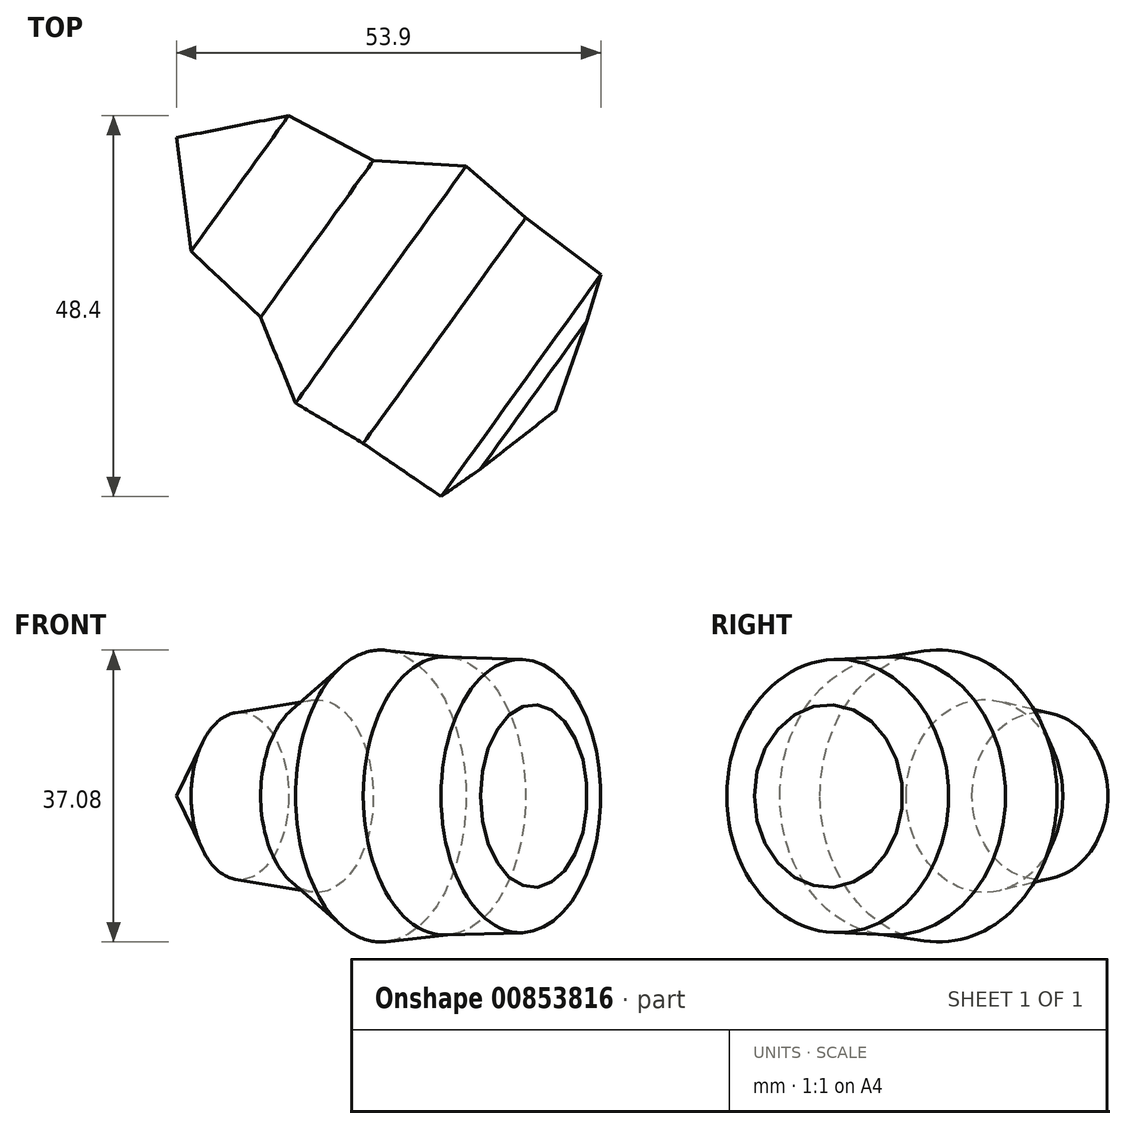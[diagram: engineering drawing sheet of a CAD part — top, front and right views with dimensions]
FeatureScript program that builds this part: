
annotation { "Feature Type Name" : "Feature", "Feature Type Description" : "" }
export const myFeature = defineFeature(function(context is Context, id is Id, definition is map)
    precondition{}
    {
        {
            var Q0;
            Q0=qCreatedBy(makeId("Top.planeOp"),FACE);
            var sketch = newSketch(context, id + "F0", { "sketchPlane" : qUnion([Q0])});
            skLineSegment(sketch, "E0", {"start": v(-33.6, 20.12) * mm, "end": v(-31.75, 5.7) * mm});
            skLineSegment(sketch, "E1", {"start": v(-31.75, 5.7) * mm, "end": v(-22.9, -2.67) * mm});
            skLineSegment(sketch, "E2", {"start": v(-22.9, -2.67) * mm, "end": v(-18.5, -13.6) * mm});
            skLineSegment(sketch, "E3", {"start": v(-18.5, -13.6) * mm, "end": v(-9.88, -18.72) * mm});
            skLineSegment(sketch, "E4", {"start": v(-9.88, -18.72) * mm, "end": v(0, -25.47) * mm});
            skLineSegment(sketch, "E5", {"start": v(0, -25.47) * mm, "end": v(5, -21.98) * mm});
            skLineSegment(sketch, "E6", {"start": v(5, -21.98) * mm, "end": v(14.54, -14.54) * mm});
            skLineSegment(sketch, "E7", {"start": v(-33.6, 20.12) * mm, "end": v(14.54, -14.54) * mm});
            skSolve(sketch);
        }
        {
            var Q0;
            Q0=makeQuery(id+"F0.imprint","IMPRINT",FACE,{"disambiguationData":[TD([[makeQuery(id+"F0.imprint","IMPRINT",EDGE,{"derivedFrom":sQuery(id+"F0.wireOp",EDGE,"E0")}),1.0]])]});
            var Q1;
            Q1=sQuery(id+"F0.wireOp",EDGE,"E7");
            revolve(context, id + "F1", {"surfaceOperationType" : NewSurfaceOperationType.NEW, "entities" : qUnion([Q0]), "axis" : qUnion([Q1]), "revolveType" : RevolveType.FULL});
        }
    });
